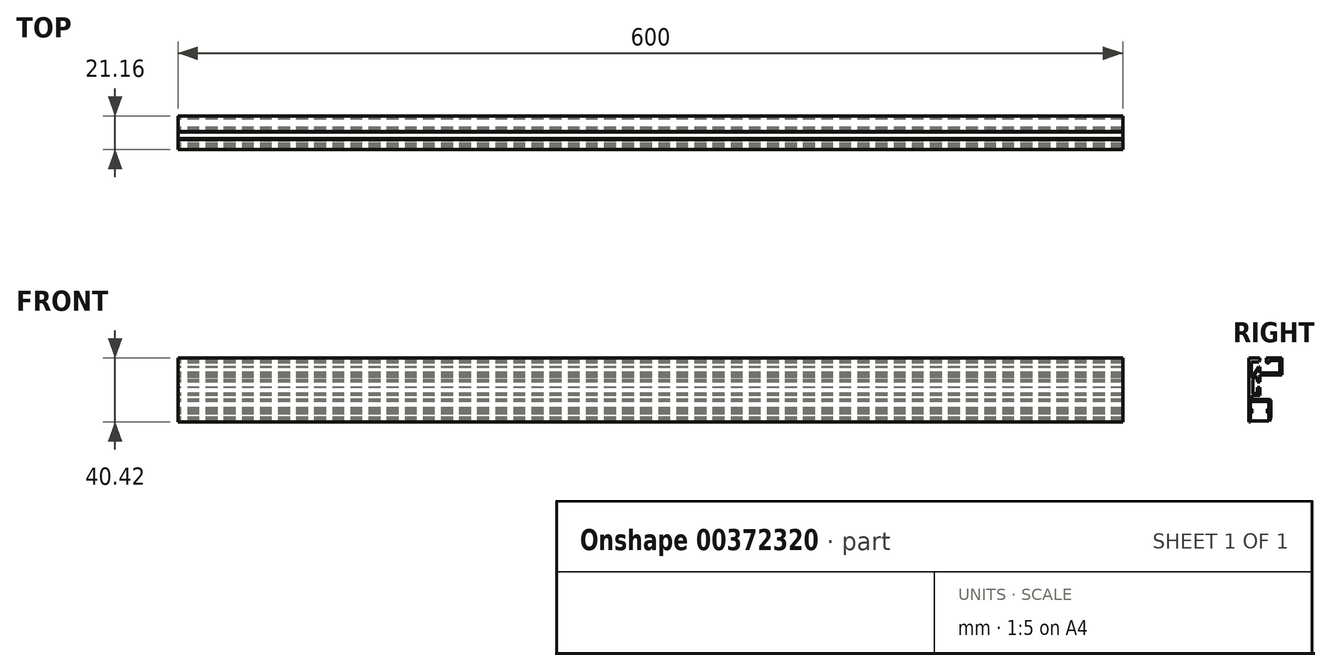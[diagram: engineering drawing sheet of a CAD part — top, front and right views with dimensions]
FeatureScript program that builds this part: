
annotation { "Feature Type Name" : "Feature", "Feature Type Description" : "" }
export const myFeature = defineFeature(function(context is Context, id is Id, definition is map)
    precondition{}
    {
        {
            var Q0;
            Q0=qCreatedBy(makeId("Right.planeOp"),FACE);
            var sketch = newSketch(context, id + "F0", { "sketchPlane" : qUnion([Q0])});
            skLineSegment(sketch, "E0.13", {"start": v(97.95, 20.2) * mm, "end": v(97.95, 9.58) * mm});
            skLineSegment(sketch, "E1.MirrorCS", {"start": v(83.74, 19.84) * mm, "end": v(83.78, 19.62) * mm});
            skLineSegment(sketch, "E2.MirrorCS", {"start": v(83.74, 18.76) * mm, "end": v(83.61, 18.51) * mm});
            skLineSegment(sketch, "E3.MirrorCS", {"start": v(83.78, 19.05) * mm, "end": v(83.74, 18.76) * mm});
            skLineSegment(sketch, "E4.MirrorCS", {"start": v(83.61, 18.51) * mm, "end": v(83.64, 18.5) * mm});
            skLineSegment(sketch, "E5.MirrorCS", {"start": v(83.2, 17.83) * mm, "end": v(83.2, 17.85) * mm});
            skLineSegment(sketch, "E6.MirrorCS", {"start": v(83.64, 18.5) * mm, "end": v(83.2, 17.83) * mm});
            skLineSegment(sketch, "E7.MirrorCS", {"start": v(83.8, 19.62) * mm, "end": v(83.8, 19.05) * mm});
            skLineSegment(sketch, "E8.MirrorCS", {"start": v(83.8, 19.05) * mm, "end": v(83.78, 19.05) * mm});
            skLineSegment(sketch, "E9.MirrorCS", {"start": v(77.92, -14.41) * mm, "end": v(77.8, -14.59) * mm});
            skLineSegment(sketch, "E10.MirrorCS", {"start": v(83.42, 20.16) * mm, "end": v(83.61, 20.04) * mm});
            skLineSegment(sketch, "E11.MirrorCS", {"start": v(82.78, 17.6) * mm, "end": v(82.78, 17.63) * mm});
            skLineSegment(sketch, "E12.MirrorCS", {"start": v(83.8, 19.62) * mm, "end": v(83.78, 19.62) * mm});
            skLineSegment(sketch, "E13.MirrorCS", {"start": v(78.16, -12.18) * mm, "end": v(78.3, -12.6) * mm});
            skLineSegment(sketch, "E14.MirrorCS", {"start": v(78.16, -14.02) * mm, "end": v(77.9, -14.41) * mm});
            skLineSegment(sketch, "E15.MirrorCS", {"start": v(83.2, 20.2) * mm, "end": v(83.42, 20.16) * mm});
            skLineSegment(sketch, "E16.MirrorCS", {"start": v(77.8, -11.61) * mm, "end": v(77.92, -11.79) * mm});
            skLineSegment(sketch, "E17.MirrorCS", {"start": v(83, 17.68) * mm, "end": v(82.78, 17.63) * mm});
            skLineSegment(sketch, "E18.MirrorCS", {"start": v(90.66, -18) * mm, "end": v(90.54, -18.5) * mm});
            skLineSegment(sketch, "E19.MirrorCS", {"start": v(78.3, -12.6) * mm, "end": v(78.36, -13.06) * mm});
            skLineSegment(sketch, "E20.MirrorCS", {"start": v(77.9, -11.79) * mm, "end": v(78.16, -12.18) * mm});
            skLineSegment(sketch, "E21.MirrorCS", {"start": v(83.2, 17.85) * mm, "end": v(83, 17.68) * mm});
            skLineSegment(sketch, "E22.MirrorCS", {"start": v(78.3, -13.6) * mm, "end": v(78.16, -14.02) * mm});
            skLineSegment(sketch, "E23.MirrorCS", {"start": v(83.61, 20.04) * mm, "end": v(83.74, 19.84) * mm});
            skLineSegment(sketch, "E24.MirrorCS", {"start": v(89.73, -14.59) * mm, "end": v(89.58, -14.41) * mm});
            skLineSegment(sketch, "E25.MirrorCS", {"start": v(90.56, -18.5) * mm, "end": v(90.54, -18.5) * mm});
            skLineSegment(sketch, "E26.MirrorCS", {"start": v(77.94, -11.74) * mm, "end": v(79.39, -13.5) * mm});
            skLineSegment(sketch, "E27.MirrorCS", {"start": v(78.36, -13.06) * mm, "end": v(78.36, -13.14) * mm});
            skLineSegment(sketch, "E28.MirrorCS", {"start": v(78.36, -13.14) * mm, "end": v(78.3, -13.6) * mm});
            skLineSegment(sketch, "E29.MirrorCS", {"start": v(77.9, -11.79) * mm, "end": v(77.92, -11.79) * mm});
            skLineSegment(sketch, "E30.MirrorCS", {"start": v(90.56, -18.5) * mm, "end": v(90.02, -20.01) * mm});
            skLineSegment(sketch, "E31.MirrorCS", {"start": v(89.58, -14.41) * mm, "end": v(89.6, -14.41) * mm});
            skLineSegment(sketch, "E32.MirrorCS", {"start": v(77.9, -14.41) * mm, "end": v(77.92, -14.41) * mm});
            skLineSegment(sketch, "E33.MirrorCS", {"start": v(89.33, -14.02) * mm, "end": v(89.19, -13.6) * mm});
            skLineSegment(sketch, "E34.MirrorCS", {"start": v(79.39, -13.5) * mm, "end": v(77.94, -15.25) * mm});
            skLineSegment(sketch, "E35.MirrorCS", {"start": v(89.58, -19.82) * mm, "end": v(89.58, -15.25) * mm});
            skLineSegment(sketch, "E36.MirrorCS", {"start": v(89.73, -20.01) * mm, "end": v(89.73, -14.59) * mm});
            skLineSegment(sketch, "E37.MirrorCS", {"start": v(89.14, -13.06) * mm, "end": v(89.14, -13.14) * mm});
            skLineSegment(sketch, "E38.MirrorCS", {"start": v(89.6, -14.41) * mm, "end": v(89.33, -14.02) * mm});
            skLineSegment(sketch, "E39.MirrorCS", {"start": v(90.02, -20.01) * mm, "end": v(89.73, -20.01) * mm});
            skLineSegment(sketch, "E40.MirrorCS", {"start": v(90.7, -6.88) * mm, "end": v(90.73, -6.88) * mm});
            skLineSegment(sketch, "E41.MirrorCS", {"start": v(89.19, -13.6) * mm, "end": v(89.14, -13.14) * mm});
            skLineSegment(sketch, "E42.MirrorCS", {"start": v(89.14, -13.06) * mm, "end": v(89.19, -12.6) * mm});
            skLineSegment(sketch, "E43.MirrorCS", {"start": v(90.68, -6.65) * mm, "end": v(90.7, -6.88) * mm});
            skLineSegment(sketch, "E44.MirrorCS", {"start": v(89.19, -12.6) * mm, "end": v(89.33, -12.18) * mm});
            skLineSegment(sketch, "E45.MirrorCS", {"start": v(89.6, -11.79) * mm, "end": v(89.58, -11.79) * mm});
            skLineSegment(sketch, "E46.MirrorCS", {"start": v(90.7, -17.5) * mm, "end": v(90.66, -18) * mm});
            skLineSegment(sketch, "E47.MirrorCS", {"start": v(89.33, -12.18) * mm, "end": v(89.6, -11.79) * mm});
            skLineSegment(sketch, "E48.MirrorCS", {"start": v(96.38, 11.05) * mm, "end": v(96.28, 10.95) * mm});
            skLineSegment(sketch, "E49.MirrorCS", {"start": v(90.41, -6.31) * mm, "end": v(90.59, -6.48) * mm});
            skLineSegment(sketch, "E50.MirrorCS", {"start": v(96.28, 10.95) * mm, "end": v(96.14, 10.9) * mm});
            skLineSegment(sketch, "E51.MirrorCS", {"start": v(89.58, -11.79) * mm, "end": v(89.73, -11.61) * mm});
            skLineSegment(sketch, "E52.MirrorCS", {"start": v(90.7, -17.5) * mm, "end": v(90.73, -17.5) * mm});
            skLineSegment(sketch, "E53.MirrorCS", {"start": v(96.43, 11.2) * mm, "end": v(96.46, 11.2) * mm});
            skLineSegment(sketch, "E54.MirrorCS", {"start": v(96.14, 10.9) * mm, "end": v(96.14, 10.88) * mm});
            skLineSegment(sketch, "E55.MirrorCS", {"start": v(96.43, 11.2) * mm, "end": v(96.38, 11.05) * mm});
            skLineSegment(sketch, "E56.MirrorCS", {"start": v(90.24, -6.21) * mm, "end": v(90.41, -6.31) * mm});
            skLineSegment(sketch, "E57.MirrorCS", {"start": v(89.58, -15.25) * mm, "end": v(88.1, -13.5) * mm});
            skLineSegment(sketch, "E58.MirrorCS", {"start": v(90.02, -6.19) * mm, "end": v(90.24, -6.21) * mm});
            skLineSegment(sketch, "E59.MirrorCS", {"start": v(90.73, -6.88) * mm, "end": v(90.73, -17.5) * mm});
            skLineSegment(sketch, "E60.MirrorCS", {"start": v(88.1, -13.5) * mm, "end": v(89.58, -11.74) * mm});
            skLineSegment(sketch, "E61.MirrorCS", {"start": v(90.02, -6.19) * mm, "end": v(90.02, -6.16) * mm});
            skLineSegment(sketch, "E62.MirrorCS", {"start": v(90.59, -6.48) * mm, "end": v(90.68, -6.65) * mm});
            skLineSegment(sketch, "E63.MirrorCS", {"start": v(89.58, -11.74) * mm, "end": v(89.58, -7.49) * mm});
            skLineSegment(sketch, "E64.MirrorCS", {"start": v(88.57, -18.8) * mm, "end": v(88.57, -15.62) * mm});
            skLineSegment(sketch, "E65.MirrorCS", {"start": v(80.7, -13.5) * mm, "end": v(78.95, -15.62) * mm});
            skLineSegment(sketch, "E66.MirrorCS", {"start": v(78.95, -11.37) * mm, "end": v(80.7, -13.5) * mm});
            skLineSegment(sketch, "E67.MirrorCS", {"start": v(87.52, -18.54) * mm, "end": v(88.57, -18.83) * mm});
            skLineSegment(sketch, "E68.MirrorCS", {"start": v(78.8, 7.96) * mm, "end": v(78.68, 7.93) * mm});
            skLineSegment(sketch, "E69.MirrorCS", {"start": v(78.53, 7.98) * mm, "end": v(78.43, 8.08) * mm});
            skLineSegment(sketch, "E70.MirrorCS", {"start": v(89.75, 17.5) * mm, "end": v(89.65, 17.36) * mm});
            skLineSegment(sketch, "E71.MirrorCS", {"start": v(89.73, -11.61) * mm, "end": v(89.73, -7.17) * mm});
            skLineSegment(sketch, "E72.MirrorCS", {"start": v(87.98, 17.36) * mm, "end": v(87.89, 17.5) * mm});
            skLineSegment(sketch, "E73.MirrorCS", {"start": v(87.81, 19.91) * mm, "end": v(87.86, 20.06) * mm});
            skLineSegment(sketch, "E74.MirrorCS", {"start": v(76.79, 20.2) * mm, "end": v(83.2, 20.2) * mm});
            skLineSegment(sketch, "E75.MirrorCS", {"start": v(87.86, 20.06) * mm, "end": v(87.96, 20.16) * mm});
            skLineSegment(sketch, "E76.MirrorCS", {"start": v(78.92, 8.05) * mm, "end": v(78.8, 7.96) * mm});
            skLineSegment(sketch, "E77.MirrorCS", {"start": v(87.81, 19.91) * mm, "end": v(87.81, 17.7) * mm});
            skLineSegment(sketch, "E78.MirrorCS", {"start": v(89.65, 17.36) * mm, "end": v(89.5, 17.26) * mm});
            skLineSegment(sketch, "E79.MirrorCS", {"start": v(83.32, 14.49) * mm, "end": v(83.61, 14.49) * mm});
            skLineSegment(sketch, "E80.MirrorCS", {"start": v(87.96, 20.16) * mm, "end": v(88.1, 20.2) * mm});
            skLineSegment(sketch, "E81.MirrorCS", {"start": v(87.89, 17.5) * mm, "end": v(87.84, 17.7) * mm});
            skLineSegment(sketch, "E82.MirrorCS", {"start": v(78.92, 8.05) * mm, "end": v(78.95, 8.05) * mm});
            skLineSegment(sketch, "E83.MirrorCS", {"start": v(88.13, 17.26) * mm, "end": v(87.98, 17.36) * mm});
            skLineSegment(sketch, "E84.MirrorCS", {"start": v(78.68, 7.93) * mm, "end": v(78.53, 7.98) * mm});
            skLineSegment(sketch, "E85.MirrorCS", {"start": v(88.33, 17.21) * mm, "end": v(89.3, 17.21) * mm});
            skLineSegment(sketch, "E86.MirrorCS", {"start": v(80.52, 8.08) * mm, "end": v(79.3, 6.24) * mm});
            skLineSegment(sketch, "E87.MirrorCS", {"start": v(77.8, -14.59) * mm, "end": v(77.8, -20.2) * mm});
            skLineSegment(sketch, "E88.MirrorCS", {"start": v(96.28, 18.66) * mm, "end": v(96.38, 18.56) * mm});
            skLineSegment(sketch, "E89.MirrorCS", {"start": v(82.78, 17.6) * mm, "end": v(78.38, 17.6) * mm});
            skLineSegment(sketch, "E90.MirrorCS", {"start": v(78.43, 8.08) * mm, "end": v(78.38, 8.23) * mm});
            skLineSegment(sketch, "E91.MirrorCS", {"start": v(88.57, -15.62) * mm, "end": v(86.8, -13.5) * mm});
            skLineSegment(sketch, "E92.MirrorCS", {"start": v(87.84, 17.7) * mm, "end": v(87.81, 17.7) * mm});
            skLineSegment(sketch, "E93.MirrorCS", {"start": v(86.8, -13.5) * mm, "end": v(88.57, -11.37) * mm});
            skLineSegment(sketch, "E94.MirrorCS", {"start": v(83.61, 14.49) * mm, "end": v(83.76, 14.44) * mm});
            skLineSegment(sketch, "E95.MirrorCS", {"start": v(88.33, 17.21) * mm, "end": v(88.13, 17.26) * mm});
            skLineSegment(sketch, "E96.MirrorCS", {"start": v(89.83, 17.7) * mm, "end": v(89.8, 17.7) * mm});
            skLineSegment(sketch, "E97.MirrorCS", {"start": v(89.5, 17.26) * mm, "end": v(89.3, 17.21) * mm});
            skLineSegment(sketch, "E98.MirrorCS", {"start": v(96.14, 18.71) * mm, "end": v(96.28, 18.66) * mm});
            skLineSegment(sketch, "E99.MirrorCS", {"start": v(78.95, -15.62) * mm, "end": v(78.95, -18.8) * mm});
            skLineSegment(sketch, "E100.MirrorCS", {"start": v(83.15, 14.39) * mm, "end": v(83.32, 14.49) * mm});
            skLineSegment(sketch, "E101.MirrorCS", {"start": v(77.94, -15.25) * mm, "end": v(77.94, -19.82) * mm});
            skLineSegment(sketch, "E102.MirrorCS", {"start": v(96.38, 18.56) * mm, "end": v(96.43, 18.42) * mm});
            skLineSegment(sketch, "E103.MirrorCS", {"start": v(77.8, -20.2) * mm, "end": v(76.79, -20.2) * mm});
            skLineSegment(sketch, "E104.MirrorCS", {"start": v(78.95, -18.83) * mm, "end": v(80, -18.54) * mm});
            skLineSegment(sketch, "E105.MirrorCS", {"start": v(88.57, -11.37) * mm, "end": v(88.57, -8.47) * mm});
            skLineSegment(sketch, "E106.MirrorCS", {"start": v(83.76, 14.44) * mm, "end": v(83.8, 14.3) * mm});
            skLineSegment(sketch, "E107.MirrorCS", {"start": v(89.83, 17.7) * mm, "end": v(89.83, 18.71) * mm});
            skLineSegment(sketch, "E108.MirrorCS", {"start": v(89.8, 17.7) * mm, "end": v(89.75, 17.5) * mm});
            skLineSegment(sketch, "E109.MirrorCS", {"start": v(77.94, -7.49) * mm, "end": v(77.94, -11.74) * mm});
            skLineSegment(sketch, "E110.MirrorCS", {"start": v(83.15, 14.39) * mm, "end": v(83.15, 14.41) * mm});
            skLineSegment(sketch, "E111.MirrorCS", {"start": v(96.43, 18.42) * mm, "end": v(96.46, 18.42) * mm});
            skLineSegment(sketch, "E112.MirrorCS", {"start": v(80, -18.54) * mm, "end": v(81.06, -18.34) * mm});
            skLineSegment(sketch, "E113.MirrorCS", {"start": v(77.8, -7.17) * mm, "end": v(77.8, -11.61) * mm});
            skLineSegment(sketch, "E114.MirrorCS", {"start": v(86.46, -18.34) * mm, "end": v(87.52, -18.54) * mm});
            skLineSegment(sketch, "E115.MirrorCS", {"start": v(80.52, 8.08) * mm, "end": v(81.4, 8.08) * mm});
            skLineSegment(sketch, "E116.MirrorCS", {"start": v(83.22, -18.12) * mm, "end": v(84.3, -18.12) * mm});
            skLineSegment(sketch, "E117.MirrorCS", {"start": v(84.3, -18.12) * mm, "end": v(85.38, -18.2) * mm});
            skLineSegment(sketch, "E118.MirrorCS", {"start": v(85.38, -18.2) * mm, "end": v(86.46, -18.34) * mm});
            skLineSegment(sketch, "E119.MirrorCS", {"start": v(78.95, -8.47) * mm, "end": v(78.95, -11.37) * mm});
            skLineSegment(sketch, "E120.MirrorCS", {"start": v(81.06, -18.34) * mm, "end": v(82.14, -18.2) * mm});
            skLineSegment(sketch, "E121.MirrorCS", {"start": v(82.14, -18.2) * mm, "end": v(83.22, -18.12) * mm});
            skLineSegment(sketch, "E122.MirrorCS", {"start": v(77.94, -19.82) * mm, "end": v(89.58, -19.82) * mm});
            skLineSegment(sketch, "E123.MirrorCS", {"start": v(82.29, 8.08) * mm, "end": v(81.4, 8.08) * mm});
            skLineSegment(sketch, "E124.MirrorCS", {"start": v(83.8, 14.3) * mm, "end": v(83.8, 10.88) * mm});
            skLineSegment(sketch, "E125.MirrorCS", {"start": v(82.29, 5.06) * mm, "end": v(82.29, 8.08) * mm});
            skLineSegment(sketch, "E126.MirrorCS", {"start": v(83.8, 5.06) * mm, "end": v(82.29, 5.06) * mm});
            skLineSegment(sketch, "E127.MirrorCS", {"start": v(89.83, 18.71) * mm, "end": v(96.14, 18.71) * mm});
            skLineSegment(sketch, "E128.MirrorCS", {"start": v(97.95, 20.2) * mm, "end": v(88.1, 20.2) * mm});
            skLineSegment(sketch, "E129.MirrorCS", {"start": v(83.8, 9.58) * mm, "end": v(83.8, 5.06) * mm});
            skLineSegment(sketch, "E130.MirrorCS", {"start": v(78.78, -3.66) * mm, "end": v(78.78, -6.16) * mm});
            skLineSegment(sketch, "E131.MirrorCS", {"start": v(82.29, -2.16) * mm, "end": v(82.29, 1.65) * mm});
            skLineSegment(sketch, "E132.MirrorCS", {"start": v(82.29, -2.16) * mm, "end": v(79.3, -2.16) * mm});
            skLineSegment(sketch, "E133.MirrorCS", {"start": v(83.8, -3.66) * mm, "end": v(78.78, -3.66) * mm});
            skLineSegment(sketch, "E134.MirrorCS", {"start": v(78.95, 8.05) * mm, "end": v(83.15, 14.41) * mm});
            skLineSegment(sketch, "E135.MirrorCS", {"start": v(82.29, 1.65) * mm, "end": v(83.8, 1.65) * mm});
            skLineSegment(sketch, "E136.MirrorCS", {"start": v(90.02, -6.16) * mm, "end": v(78.78, -6.16) * mm});
            skLineSegment(sketch, "E137.MirrorCS", {"start": v(83.8, 1.65) * mm, "end": v(83.8, -3.66) * mm});
            skLineSegment(sketch, "E138.MirrorCS", {"start": v(76.79, 20.2) * mm, "end": v(76.79, -20.2) * mm});
            skLineSegment(sketch, "E139.MirrorCS", {"start": v(77.8, -7.17) * mm, "end": v(89.73, -7.17) * mm});
            skPoint(sketch, "E140.MirrorP", {"position": v(89.11, -13.14) * mm});
            skLineSegment(sketch, "E141.MirrorCS", {"start": v(79.3, 6.24) * mm, "end": v(79.3, -2.16) * mm});
            skLineSegment(sketch, "E142.MirrorCS", {"start": v(83.8, 10.88) * mm, "end": v(96.14, 10.88) * mm});
            skLineSegment(sketch, "E143.MirrorCS", {"start": v(89.58, -7.49) * mm, "end": v(77.94, -7.49) * mm});
            skLineSegment(sketch, "E144.MirrorCS", {"start": v(88.57, -8.47) * mm, "end": v(78.95, -8.47) * mm});
            skPoint(sketch, "E145.MirrorP", {"position": v(82.29, 8.08) * mm});
            skLineSegment(sketch, "E146.MirrorCS", {"start": v(83.8, 9.58) * mm, "end": v(97.95, 9.58) * mm});
            skLineSegment(sketch, "E147.MirrorCS", {"start": v(78.38, 17.6) * mm, "end": v(78.38, 8.23) * mm});
            skPoint(sketch, "E148.MirrorP", {"position": v(89.11, -13.06) * mm});
            skPoint(sketch, "E149.MirrorP", {"position": v(83.05, 5.06) * mm});
            skLineSegment(sketch, "E150.MirrorCS", {"start": v(96.46, 18.42) * mm, "end": v(96.46, 11.2) * mm});
            skPoint(sketch, "E151.MirrorP", {"position": v(81.4, 8.08) * mm});
            skSolve(sketch);
        }
        {
            var Q0;
            Q0 = qSketchRegion(id + "F0", true);
            extrude(context, id + "F1", {"entities" : qUnion([Q0]), "offsetDistance" : 25 * mm, "depth" : 600 * mm});
        }
    });
